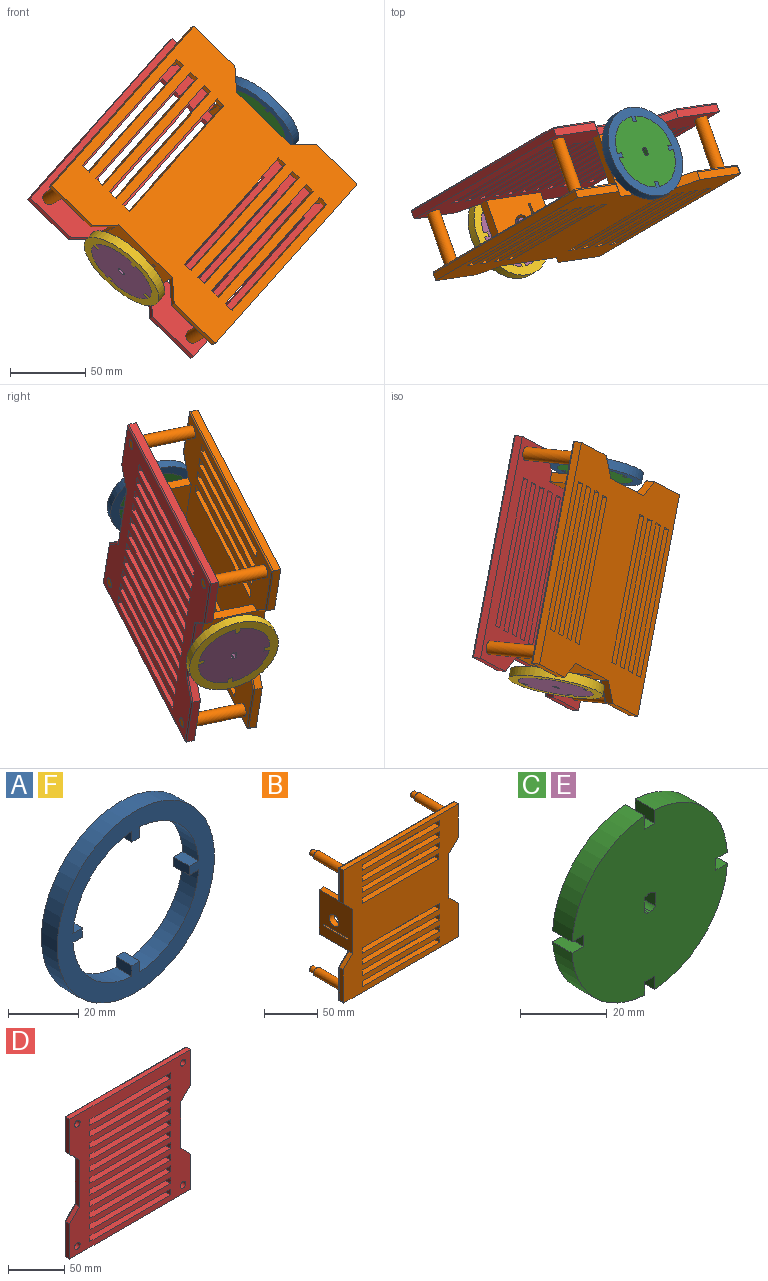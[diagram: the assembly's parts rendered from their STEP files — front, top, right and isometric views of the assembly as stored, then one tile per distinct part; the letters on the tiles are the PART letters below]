
ASSEMBLY  parts=6 mates=6
PART A: 19 faces, bbox 63.5x6.4x63.5 mm
  f0: plane 6.35x3.76mm, normal (1,0,0), area 23.9mm2, adj f1,f4,f17,f18
  f1: plane 6.35x3.18mm, normal (0,0,-1), area 20.2mm2, adj f0,f2,f17,f18
  f2: plane 6.35x3.76mm, normal (-1,0,0), area 23.9mm2, adj f1,f3,f17,f18
  f3: cylinder r=25.4mm len=23.76mm, axis (0,1,0), area 233.2mm2, adj f2,f5,f17,f18
  f4: cylinder r=25.4mm len=23.76mm, axis (0,1,0), area 233.2mm2, adj f0,f11,f17,f18
  f5: plane 6.35x3.76mm, normal (0,0,1), area 23.9mm2, adj f3,f6,f17,f18
  f6: plane 6.35x3.18mm, normal (1,0,0), area 20.2mm2, adj f5,f7,f17,f18
  f7: plane 6.35x3.76mm, normal (0,0,-1), area 23.9mm2, adj f6,f8,f17,f18
  f8: cylinder r=25.4mm len=23.76mm, axis (0,1,0), area 233.2mm2, adj f7,f13,f17,f18
  f9: plane 6.35x3.76mm, normal (0,0,-1), area 23.9mm2, adj f10,f12,f17,f18
  f10: plane 6.35x3.18mm, normal (-1,0,0), area 20.2mm2, adj f9,f11,f17,f18
  f11: plane 6.35x3.76mm, normal (0,0,1), area 23.9mm2, adj f4,f10,f17,f18
  f12: cylinder r=25.4mm len=23.76mm, axis (0,1,0), area 233.2mm2, adj f9,f15,f17,f18
  f13: plane 6.35x3.76mm, normal (-1,0,0), area 23.9mm2, adj f8,f14,f17,f18
  f14: plane 6.35x3.18mm, normal (0,0,1), area 20.2mm2, adj f13,f15,f17,f18
  f15: plane 6.35x3.76mm, normal (1,0,0), area 23.9mm2, adj f12,f14,f17,f18
  f16: cylinder r=31.75mm len=63.5mm, axis (0,1,0), area 1266.8mm2, adj f17,f18
  f17: plane 63.5x63.5mm, normal (0,1,0), area 1188.3mm2, adj f0,f1,f2,f3,f4,f5,f6,f7
  f18: plane 63.5x63.5mm, normal (0,-1,0), area 1188.3mm2, adj f0,f1,f2,f3,f4,f5,f6,f7
PART B: 95 faces, bbox 152.4x50.8x152.4 mm
  f0: cylinder r=1mm len=5.35mm, axis (0,1,0), area 8.4mm2, adj f2,f5,f6,f20
  f1: cylinder r=1mm len=150.4mm, axis (-1,0,0), area 236.2mm2, adj f2,f4,f8,f20
  f2: sphere r=1mm, area 1.6mm2, adj f0,f1,f7
  f3: cylinder r=1mm len=5.35mm, axis (0,1,0), area 8.4mm2, adj f4,f5,f20,f76
  f4: sphere r=1mm, area 1.6mm2, adj f1,f3,f22
  f5: plane 152.4x152.4mm, normal (0,-1,0), area 16470.3mm2, adj f0,f3,f6,f14,f15,f16,f17,f18
  f6: plane 37.3x5.35mm, normal (1,0,0), area 199.6mm2, adj f0,f5,f7,f26
  f7: cylinder r=1mm len=38.3mm, axis (0,0,-1), area 59.2mm2, adj f2,f6,f8,f26
  f8: plane 150.4x150.4mm, normal (0,1,0), area 15093.7mm2, adj f1,f7,f9,f10,f11,f12,f13,f21
  f9: cylinder r=1mm len=13.85mm, axis (0.71,0,0.71), area 28mm2, adj f8,f10,f14,f25,f86,f93
  f10: cylinder r=1mm len=38.37mm, axis (0,0,-1), area 59.5mm2, adj f8,f9,f11,f15
  f11: cylinder r=1mm len=152.4mm, axis (1,0,0), area 238.2mm2, adj f8,f10,f12,f16
  f12: cylinder r=1mm len=38.37mm, axis (0,0,1), area 59.5mm2, adj f8,f11,f13,f17
  f13: cylinder r=1mm len=13.85mm, axis (0.71,0,-0.71), area 28mm2, adj f8,f12,f18,f19,f87,f89
  f14: plane 12.5x12.5mm, normal (0.71,0,-0.71), area 94.6mm2, adj f5,f9,f15,f25
  f15: plane 38.37x5.35mm, normal (1,0,0), area 205.3mm2, adj f5,f10,f14,f16
  f16: plane 152.4x5.35mm, normal (0,0,1), area 815.3mm2, adj f5,f11,f15,f17
  f17: plane 38.37x5.35mm, normal (-1,0,0), area 205.3mm2, adj f5,f12,f16,f18
  f18: plane 12.5x12.5mm, normal (-0.71,0,-0.71), area 94.6mm2, adj f5,f13,f17,f19
  f19: plane 5.86x0.2mm, normal (0,0,-1), area 1.1mm2, adj f5,f13,f18,f87
  f20: plane 150.4x5.35mm, normal (0,0,-1), area 804.6mm2, adj f0,f1,f3,f5
  f21: cylinder r=1mm len=13.91mm, axis (-0.71,0,-0.71), area 28.1mm2, adj f8,f22,f23,f24,f88
  f22: cylinder r=1mm len=37.3mm, axis (0,0,1), area 58.4mm2, adj f4,f8,f21,f76
  f23: plane 5.86x0.2mm, normal (0,0,1), area 1.1mm2, adj f5,f21,f24,f87
  f24: plane 12.5x12.5mm, normal (-0.71,0,0.71), area 94.6mm2, adj f5,f21,f23,f76
  f25: plane 5.86x0.2mm, normal (0,0,-1), area 1.1mm2, adj f5,f9,f14,f86
  f26: plane 12.5x12.5mm, normal (0.71,0,0.71), area 111.9mm2, adj f5,f6,f7,f8,f27
  f27: plane 6.35x0.2mm, normal (0,0,1), area 1.3mm2, adj f5,f8,f26,f86
  f28: plane 6.35x6.35mm, normal (1,0,0), area 40.3mm2, adj f5,f8,f29,f31
  f29: plane 101.6x6.35mm, normal (0,0,-1), area 645.2mm2, adj f5,f8,f28,f30
  f30: plane 6.35x6.35mm, normal (-1,0,0), area 40.3mm2, adj f5,f8,f29,f31
  f31: plane 101.6x6.35mm, normal (0,0,1), area 645.2mm2, adj f5,f8,f28,f30
  f32: plane 6.49x6.35mm, normal (1,0,0), area 41.2mm2, adj f5,f8,f33,f35
  f33: plane 101.6x6.35mm, normal (0,0,-1), area 645.2mm2, adj f5,f8,f32,f34
  f34: plane 6.49x6.35mm, normal (-1,0,0), area 41.2mm2, adj f5,f8,f33,f35
  f35: plane 101.6x6.35mm, normal (0,0,1), area 645.2mm2, adj f5,f8,f32,f34
  f36: plane 6.35x6.35mm, normal (1,0,0), area 40.3mm2, adj f5,f8,f37,f39
  f37: plane 101.6x6.35mm, normal (0,0,-1), area 645.2mm2, adj f5,f8,f36,f38
  f38: plane 6.35x6.35mm, normal (-1,0,0), area 40.3mm2, adj f5,f8,f37,f39
  f39: plane 101.6x6.35mm, normal (0,0,1), area 645.2mm2, adj f5,f8,f36,f38
  f40: plane 6.35x6.16mm, normal (1,0,0), area 39.1mm2, adj f5,f8,f41,f43
  f41: plane 101.6x6.35mm, normal (0,0,-1), area 645.2mm2, adj f5,f8,f40,f42
  f42: plane 6.35x6.16mm, normal (-1,0,0), area 39.1mm2, adj f5,f8,f41,f43
  f43: plane 101.6x6.35mm, normal (0,0,1), area 645.2mm2, adj f5,f8,f40,f42
  f44: plane 6.35x6.35mm, normal (1,0,0), area 40.3mm2, adj f5,f8,f45,f47
  f45: plane 101.6x6.35mm, normal (0,0,-1), area 645.2mm2, adj f5,f8,f44,f46
  f46: plane 6.35x6.35mm, normal (-1,0,0), area 40.3mm2, adj f5,f8,f45,f47
  f47: plane 101.6x6.35mm, normal (0,0,1), area 645.2mm2, adj f5,f8,f44,f46
  f48: plane 6.35x6.35mm, normal (1,0,0), area 40.3mm2, adj f5,f8,f49,f51
  f49: plane 101.6x6.35mm, normal (0,0,-1), area 645.2mm2, adj f5,f8,f48,f50
  f50: plane 6.35x6.35mm, normal (-1,0,0), area 40.3mm2, adj f5,f8,f49,f51
  f51: plane 101.6x6.35mm, normal (0,0,1), area 645.2mm2, adj f5,f8,f48,f50
  f52: plane 6.35x6.35mm, normal (1,0,0), area 40.3mm2, adj f5,f8,f53,f55
  f53: plane 101.6x6.35mm, normal (0,0,-1), area 645.2mm2, adj f5,f8,f52,f54
  f54: plane 6.35x6.35mm, normal (-1,0,0), area 40.3mm2, adj f5,f8,f53,f55
  f55: plane 101.6x6.35mm, normal (0,0,1), area 645.2mm2, adj f5,f8,f52,f54
  f56: plane 6.35x6.35mm, normal (1,0,0), area 40.3mm2, adj f5,f8,f57,f59
  f57: plane 101.18x6.35mm, normal (0,0,-1), area 642.5mm2, adj f5,f8,f56,f58
  f58: plane 6.35x6.35mm, normal (-1,0,0), area 40.3mm2, adj f5,f8,f57,f59
  f59: plane 101.18x6.35mm, normal (0,0,1), area 642.5mm2, adj f5,f8,f56,f58
  f60: cylinder r=3.17mm len=6.35mm, axis (0,1,0), area 126.7mm2, adj f61,f71
  f61: plane 6.35x6.35mm, normal (0,1,0), area 31.7mm2, adj f60
  f62: cylinder r=3.17mm len=6.35mm, axis (0,1,0), area 126.7mm2, adj f63,f69
  f63: plane 6.35x6.35mm, normal (0,1,0), area 31.7mm2, adj f62
  f64: cylinder r=3.17mm len=6.35mm, axis (0,1,0), area 126.7mm2, adj f65,f75
  f65: plane 6.35x6.35mm, normal (0,1,0), area 31.7mm2, adj f64
  f66: cylinder r=3.17mm len=6.35mm, axis (0,1,0), area 126.7mm2, adj f67,f73
  f67: plane 6.35x6.35mm, normal (0,1,0), area 31.7mm2, adj f66
  f68: cylinder r=4.45mm len=38.1mm, axis (0,1,0), area 1064.1mm2, adj f8,f69
  f69: plane 8.89x8.89mm, normal (0,1,0), area 30.4mm2, adj f62,f68
  f70: cylinder r=4.45mm len=38.1mm, axis (0,1,0), area 1064.1mm2, adj f8,f71
  f71: plane 8.89x8.89mm, normal (0,1,0), area 30.4mm2, adj f60,f70
  f72: cylinder r=4.45mm len=38.1mm, axis (0,1,0), area 1064.1mm2, adj f8,f73
  f73: plane 8.89x8.89mm, normal (0,1,0), area 30.4mm2, adj f66,f72
  f74: cylinder r=4.45mm len=38.1mm, axis (0,1,0), area 1064.1mm2, adj f8,f75
  f75: plane 8.89x8.89mm, normal (0,1,0), area 30.4mm2, adj f64,f74
  f76: plane 37.3x5.35mm, normal (-1,0,0), area 199.6mm2, adj f3,f5,f22,f24
  f77: cylinder r=6.35mm len=12.7mm, axis (-1,0,0), area 253.4mm2, adj f86,f91
  f78: cylinder r=6.35mm len=12.7mm, axis (-1,0,0), area 253.4mm2, adj f85,f87
  f79: plane 31.75x6.35mm, normal (0,0,-1), area 201.6mm2, adj f8,f80,f86,f91
  f80: plane 6.35x1.91mm, normal (0,-1,0), area 12.1mm2, adj f79,f81,f86,f91
  f81: plane 31.75x6.35mm, normal (0,0,1), area 201.6mm2, adj f8,f80,f86,f91
  f82: plane 31.75x6.35mm, normal (0,0,1), area 201.6mm2, adj f8,f83,f85,f87
  f83: plane 6.35x1.91mm, normal (0,-1,0), area 12.1mm2, adj f82,f84,f85,f87
  f84: plane 31.75x6.35mm, normal (0,0,-1), area 201.6mm2, adj f8,f83,f85,f87
  f85: plane 50.8x38.1mm, normal (1,0,0), area 1748.3mm2, adj f8,f78,f82,f83,f84,f88,f89,f90
  f86: plane 50.8x44.45mm, normal (1,0,0), area 2070.5mm2, adj f5,f8,f9,f25,f27,f77,f79,f80
  f87: plane 50.8x44.45mm, normal (-1,0,0), area 2070.5mm2, adj f5,f8,f13,f19,f23,f78,f82,f83
  f88: plane 38.59x6.35mm, normal (0,0,-1), area 242.1mm2, adj f8,f21,f85,f87,f90
  f89: plane 38.52x6.35mm, normal (0,0,1), area 242.1mm2, adj f8,f13,f85,f87,f90
  f90: plane 50.8x6.35mm, normal (0,1,0), area 322.6mm2, adj f85,f87,f88,f89
  f91: plane 50.8x38.1mm, normal (-1,0,0), area 1748.3mm2, adj f8,f77,f79,f80,f81,f92,f93,f94
  f92: plane 38.1x6.35mm, normal (0,0,-1), area 241.9mm2, adj f8,f86,f91,f94
  f93: plane 38.52x6.35mm, normal (0,0,1), area 242.1mm2, adj f8,f9,f86,f91,f94
  f94: plane 50.8x6.35mm, normal (0,1,0), area 322.6mm2, adj f86,f91,f92,f93
PART C: 28 faces, bbox 50.7x19.1x50.7 mm
  f0: plane 19.05x3.79mm, normal (1,0,0), area 72.2mm2, adj f1,f7,f9,f22
  f1: cylinder r=2.46mm len=19.05mm, axis (0,-1,0), area 30.8mm2, adj f0,f2,f9,f22
  f2: plane 19.05x0.76mm, normal (0,0,-1), area 14.4mm2, adj f1,f3,f9,f22
  f3: cylinder r=2.46mm len=19.05mm, axis (0,-1,0), area 30.4mm2, adj f2,f4,f9,f22
  f4: plane 19.05x3.83mm, normal (-1,0,0), area 72.9mm2, adj f3,f5,f9,f22
  f5: cylinder r=2.34mm len=19.05mm, axis (0,-1,0), area 32.1mm2, adj f4,f6,f9,f22
  f6: plane 19.05x0.65mm, normal (0,0,1), area 12.3mm2, adj f5,f7,f9,f22
  f7: cylinder r=2.34mm len=19.05mm, axis (0,-1,0), area 32.5mm2, adj f0,f6,f9,f22
  f8: cylinder r=4.45mm len=12.7mm, axis (0,1,0), area 354.7mm2, adj f9,f27
  f9: plane 8.89x8.89mm, normal (0,1,0), area 44.7mm2, adj f0,f1,f2,f3,f4,f5,f6,f7
  f10: plane 6.35x3.18mm, normal (1,0,0), area 20.2mm2, adj f11,f12,f22,f27
  f11: plane 6.35x3.76mm, normal (0,0,-1), area 23.9mm2, adj f10,f22,f25,f27
  f12: plane 6.35x3.76mm, normal (0,0,1), area 23.9mm2, adj f10,f22,f26,f27
  f13: plane 6.35x3.18mm, normal (0,0,1), area 20.2mm2, adj f14,f15,f22,f27
  f14: plane 6.35x3.76mm, normal (1,0,0), area 23.9mm2, adj f13,f22,f24,f27
  f15: plane 6.35x3.76mm, normal (-1,0,0), area 23.9mm2, adj f13,f22,f25,f27
  f16: plane 6.35x3.76mm, normal (-1,0,0), area 23.9mm2, adj f18,f22,f26,f27
  f17: plane 6.35x3.76mm, normal (1,0,0), area 23.9mm2, adj f18,f22,f23,f27
  f18: plane 6.35x3.18mm, normal (0,0,-1), area 20.2mm2, adj f16,f17,f22,f27
  f19: plane 6.35x3.18mm, normal (-1,0,0), area 20.2mm2, adj f20,f21,f22,f27
  f20: plane 6.35x3.76mm, normal (0,0,1), area 23.9mm2, adj f19,f22,f23,f27
  f21: plane 6.35x3.76mm, normal (0,0,-1), area 23.9mm2, adj f19,f22,f24,f27
  f22: plane 50.7x50.7mm, normal (0,-1,0), area 1961.3mm2, adj f0,f1,f2,f3,f4,f5,f6,f7
  f23: cylinder r=25.4mm len=23.76mm, axis (0,1,0), area 233.2mm2, adj f17,f20,f22,f27
  f24: cylinder r=25.4mm len=23.76mm, axis (0,1,0), area 233.2mm2, adj f14,f21,f22,f27
  f25: cylinder r=25.4mm len=23.76mm, axis (0,1,0), area 233.2mm2, adj f11,f15,f22,f27
  f26: cylinder r=25.4mm len=23.76mm, axis (0,1,0), area 233.2mm2, adj f12,f16,f22,f27
  f27: plane 50.7x50.7mm, normal (0,1,0), area 1916.6mm2, adj f8,f10,f11,f12,f13,f14,f15,f16
PART D: 74 faces, bbox 152.4x6.4x152.4 mm
  f0: cylinder r=1mm len=152.4mm, axis (1,0,0), area 238.2mm2, adj f1,f11,f17,f18
  f1: cylinder r=1mm len=38.3mm, axis (0,0,1), area 59.4mm2, adj f0,f2,f18,f72
  f2: cylinder r=1mm len=13.5mm, axis (0.71,0,-0.71), area 27.8mm2, adj f1,f3,f18,f20
  f3: cylinder r=1mm len=51.63mm, axis (0,0,-1), area 80.3mm2, adj f2,f4,f18,f19
  f4: cylinder r=1mm len=13.5mm, axis (-0.71,0,-0.71), area 27.8mm2, adj f3,f5,f18,f21
  f5: cylinder r=1mm len=38.3mm, axis (0,0,1), area 59.4mm2, adj f4,f6,f18,f22
  f6: cylinder r=1mm len=152.4mm, axis (-1,0,0), area 238.2mm2, adj f5,f7,f18,f73
  f7: cylinder r=1mm len=38.3mm, axis (0,0,-1), area 59.4mm2, adj f6,f8,f12,f18
  f8: cylinder r=1mm len=13.5mm, axis (-0.71,0,0.71), area 27.8mm2, adj f7,f9,f13,f18
  f9: cylinder r=1mm len=51.63mm, axis (0,0,-1), area 80.3mm2, adj f8,f10,f14,f18
  f10: cylinder r=1mm len=13.5mm, axis (0.71,0,0.71), area 27.8mm2, adj f9,f11,f15,f18
  f11: cylinder r=1mm len=38.3mm, axis (0,0,-1), area 59.4mm2, adj f0,f10,f16,f18
  f12: plane 38.3x5.35mm, normal (1,0,0), area 204.9mm2, adj f7,f13,f23,f73
  f13: plane 12.5x12.5mm, normal (0.71,0,0.71), area 94.6mm2, adj f8,f12,f14,f23
  f14: plane 50.8x5.35mm, normal (1,0,0), area 271.8mm2, adj f9,f13,f15,f23
  f15: plane 12.5x12.5mm, normal (0.71,0,-0.71), area 94.6mm2, adj f10,f14,f16,f23
  f16: plane 38.3x5.35mm, normal (1,0,0), area 204.9mm2, adj f11,f15,f17,f23
  f17: plane 152.4x5.35mm, normal (0,0,1), area 815.3mm2, adj f0,f16,f23,f72
  f18: plane 150.4x150.4mm, normal (0,1,0), area 13780.1mm2, adj f0,f1,f2,f3,f4,f5,f6,f7
  f19: plane 50.8x5.35mm, normal (-1,0,0), area 271.8mm2, adj f3,f20,f21,f23
  f20: plane 12.5x12.5mm, normal (-0.71,0,-0.71), area 94.6mm2, adj f2,f19,f23,f72
  f21: plane 12.5x12.5mm, normal (-0.71,0,0.71), area 94.6mm2, adj f4,f19,f22,f23
  f22: plane 38.3x5.35mm, normal (-1,0,0), area 204.9mm2, adj f5,f21,f23,f73
  f23: plane 152.4x152.4mm, normal (0,-1,0), area 14406.4mm2, adj f12,f13,f14,f15,f16,f17,f19,f20
  f24: plane 6.35x6.35mm, normal (1,0,0), area 40.3mm2, adj f18,f23,f25,f27
  f25: plane 101.6x6.35mm, normal (0,0,-1), area 645.2mm2, adj f18,f23,f24,f26
  f26: plane 6.35x6.35mm, normal (-1,0,0), area 40.3mm2, adj f18,f23,f25,f27
  f27: plane 101.6x6.35mm, normal (0,0,1), area 645.2mm2, adj f18,f23,f24,f26
  f28: plane 6.35x6.35mm, normal (1,0,0), area 40.3mm2, adj f18,f23,f29,f31
  f29: plane 101.6x6.35mm, normal (0,0,-1), area 645.2mm2, adj f18,f23,f28,f30
  f30: plane 6.35x6.35mm, normal (-1,0,0), area 40.3mm2, adj f18,f23,f29,f31
  f31: plane 101.6x6.35mm, normal (0,0,1), area 645.2mm2, adj f18,f23,f28,f30
  f32: plane 6.35x6.35mm, normal (1,0,0), area 40.3mm2, adj f18,f23,f33,f35
  f33: plane 101.6x6.35mm, normal (0,0,-1), area 645.2mm2, adj f18,f23,f32,f34
  f34: plane 6.35x6.35mm, normal (-1,0,0), area 40.3mm2, adj f18,f23,f33,f35
  f35: plane 101.6x6.35mm, normal (0,0,1), area 645.2mm2, adj f18,f23,f32,f34
  f36: plane 6.35x6.35mm, normal (1,0,0), area 40.3mm2, adj f18,f23,f37,f39
  f37: plane 101.6x6.35mm, normal (0,0,-1), area 645.2mm2, adj f18,f23,f36,f38
  f38: plane 6.35x6.35mm, normal (-1,0,0), area 40.3mm2, adj f18,f23,f37,f39
  f39: plane 101.6x6.35mm, normal (0,0,1), area 645.2mm2, adj f18,f23,f36,f38
  f40: plane 6.35x6.35mm, normal (1,0,0), area 40.3mm2, adj f18,f23,f41,f43
  f41: plane 101.6x6.35mm, normal (0,0,-1), area 645.2mm2, adj f18,f23,f40,f42
  f42: plane 6.35x6.35mm, normal (-1,0,0), area 40.3mm2, adj f18,f23,f41,f43
  f43: plane 101.6x6.35mm, normal (0,0,1), area 645.2mm2, adj f18,f23,f40,f42
  f44: plane 6.35x6.35mm, normal (1,0,0), area 40.3mm2, adj f18,f23,f45,f47
  f45: plane 101.6x6.35mm, normal (0,0,-1), area 645.2mm2, adj f18,f23,f44,f46
  f46: plane 6.35x6.35mm, normal (-1,0,0), area 40.3mm2, adj f18,f23,f45,f47
  f47: plane 101.6x6.35mm, normal (0,0,1), area 645.2mm2, adj f18,f23,f44,f46
  f48: plane 6.35x6.35mm, normal (1,0,0), area 40.3mm2, adj f18,f23,f49,f51
  f49: plane 101.6x6.35mm, normal (0,0,-1), area 645.2mm2, adj f18,f23,f48,f50
  f50: plane 6.35x6.35mm, normal (-1,0,0), area 40.3mm2, adj f18,f23,f49,f51
  f51: plane 101.6x6.35mm, normal (0,0,1), area 645.2mm2, adj f18,f23,f48,f50
  f52: plane 6.35x6.27mm, normal (1,0,0), area 39.8mm2, adj f18,f23,f53,f55
  f53: plane 101.6x6.35mm, normal (0,0,-1), area 645.2mm2, adj f18,f23,f52,f54
  f54: plane 6.35x6.27mm, normal (-1,0,0), area 39.8mm2, adj f18,f23,f53,f55
  f55: plane 101.6x6.35mm, normal (0,0,1), area 645.2mm2, adj f18,f23,f52,f54
  f56: plane 6.35x6.35mm, normal (1,0,0), area 40.3mm2, adj f18,f23,f57,f59
  f57: plane 101.6x6.35mm, normal (0,0,-1), area 645.2mm2, adj f18,f23,f56,f58
  f58: plane 6.35x6.35mm, normal (-1,0,0), area 40.3mm2, adj f18,f23,f57,f59
  f59: plane 101.6x6.35mm, normal (0,0,1), area 645.2mm2, adj f18,f23,f56,f58
  f60: plane 6.35x6.35mm, normal (1,0,0), area 40.3mm2, adj f18,f23,f61,f63
  f61: plane 101.6x6.35mm, normal (0,0,-1), area 645.2mm2, adj f18,f23,f60,f62
  f62: plane 6.35x6.35mm, normal (-1,0,0), area 40.3mm2, adj f18,f23,f61,f63
  f63: plane 101.6x6.35mm, normal (0,0,1), area 645.2mm2, adj f18,f23,f60,f62
  f64: plane 6.35x6.35mm, normal (1,0,0), area 40.3mm2, adj f18,f23,f65,f67
  f65: plane 101.6x6.35mm, normal (0,0,-1), area 645.2mm2, adj f18,f23,f64,f66
  f66: plane 6.35x6.35mm, normal (-1,0,0), area 40.3mm2, adj f18,f23,f65,f67
  f67: plane 101.6x6.35mm, normal (0,0,1), area 645.2mm2, adj f18,f23,f64,f66
  f68: cylinder r=3.43mm len=6.86mm, axis (0,-1,0), area 136.8mm2, adj f18,f23
  f69: cylinder r=3.43mm len=6.86mm, axis (0,-1,0), area 136.8mm2, adj f18,f23
  f70: cylinder r=3.43mm len=6.86mm, axis (0,-1,0), area 136.8mm2, adj f18,f23
  f71: cylinder r=3.43mm len=6.86mm, axis (0,-1,0), area 136.8mm2, adj f18,f23
  f72: plane 38.3x5.35mm, normal (-1,0,0), area 204.9mm2, adj f1,f17,f20,f23
  f73: plane 152.4x5.35mm, normal (0,0,-1), area 815.3mm2, adj f6,f12,f22,f23
PART E: same geometry as C
PART F: same geometry as A
PLACE A rot(axis=(0.34,-0.55,0.76),160.4deg) t=(125.72,91.12,118.53)mm
PLACE B rot(axis=(-0.05,-0.9,0.44),51.8deg) t=(91.53,9.99,-34.94)mm
PLACE C rot(axis=(0.34,-0.55,0.76),160.4deg) t=(124.94,89.05,120.3)mm
PLACE D rot(axis=(-0.05,-0.9,0.44),51.8deg) t=(77.09,51.16,-43.44)mm
PLACE E rot(axis=(0.41,-0.46,-0.79),79.1deg) t=(31.73,34.17,12.92)mm
PLACE F rot(axis=(0.41,-0.46,-0.79),79.1deg) t=(32.51,36.24,11.16)mm
MATE fastened E.f8 <-> F.f3  axis (0.62,0.36,0.7) through (30.59,27.04,22.2)mm
MATE fastened C.f9 <-> B.f77  axis (-0.62,-0.36,-0.7) through (111.3,74.06,112.87)mm
MATE fastened D.f68 <-> B.f66  axis (-0.32,0.93,-0.19) through (156.33,108.88,68.4)mm
MATE fastened C.f8 <-> A.f3  axis (-0.62,-0.36,-0.7) through (119.86,79.63,125.15)mm
MATE fastened E.f8 <-> B.f77  axis (0.62,0.36,0.7) through (40.43,32.77,33.25)mm
MATE fastened C.f8 <-> B.f77  axis (-0.62,-0.36,-0.7) through (110.01,73.9,114.09)mm
